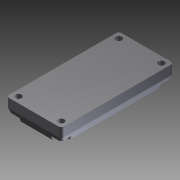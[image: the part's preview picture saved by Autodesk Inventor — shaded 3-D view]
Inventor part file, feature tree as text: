
AUTODESK INVENTOR PART (.ipt)
format: ipt  version: 2015 (Build 190159000, 159)  size: 187,904 bytes
history: native  units: in
note: dims shown in document units (in); Inventor stores cm internally (conversion verified against a paired STEP export)
features: fillet x1, other x1, imported_body x1
ambient origin geometry x8: Origin, YZ Plane, XZ Plane, XY Plane, X Axis, Y Axis, Z Axis, Center Point
bodies: Body1 (feature_tree)
feature tree (3):
  fillet  "Fillet2"  [1 undecoded]
  other  "TOWER PRO MG-995, ANALOG SERVO, BODY, BOTTOM.ipt1"
  imported_body  "Base1"
note: 1 required parameter value undecoded (feature->parameter linkage not recoverable at this tier; creation-order binding heuristic only, values carry confidence <= 0.55)
